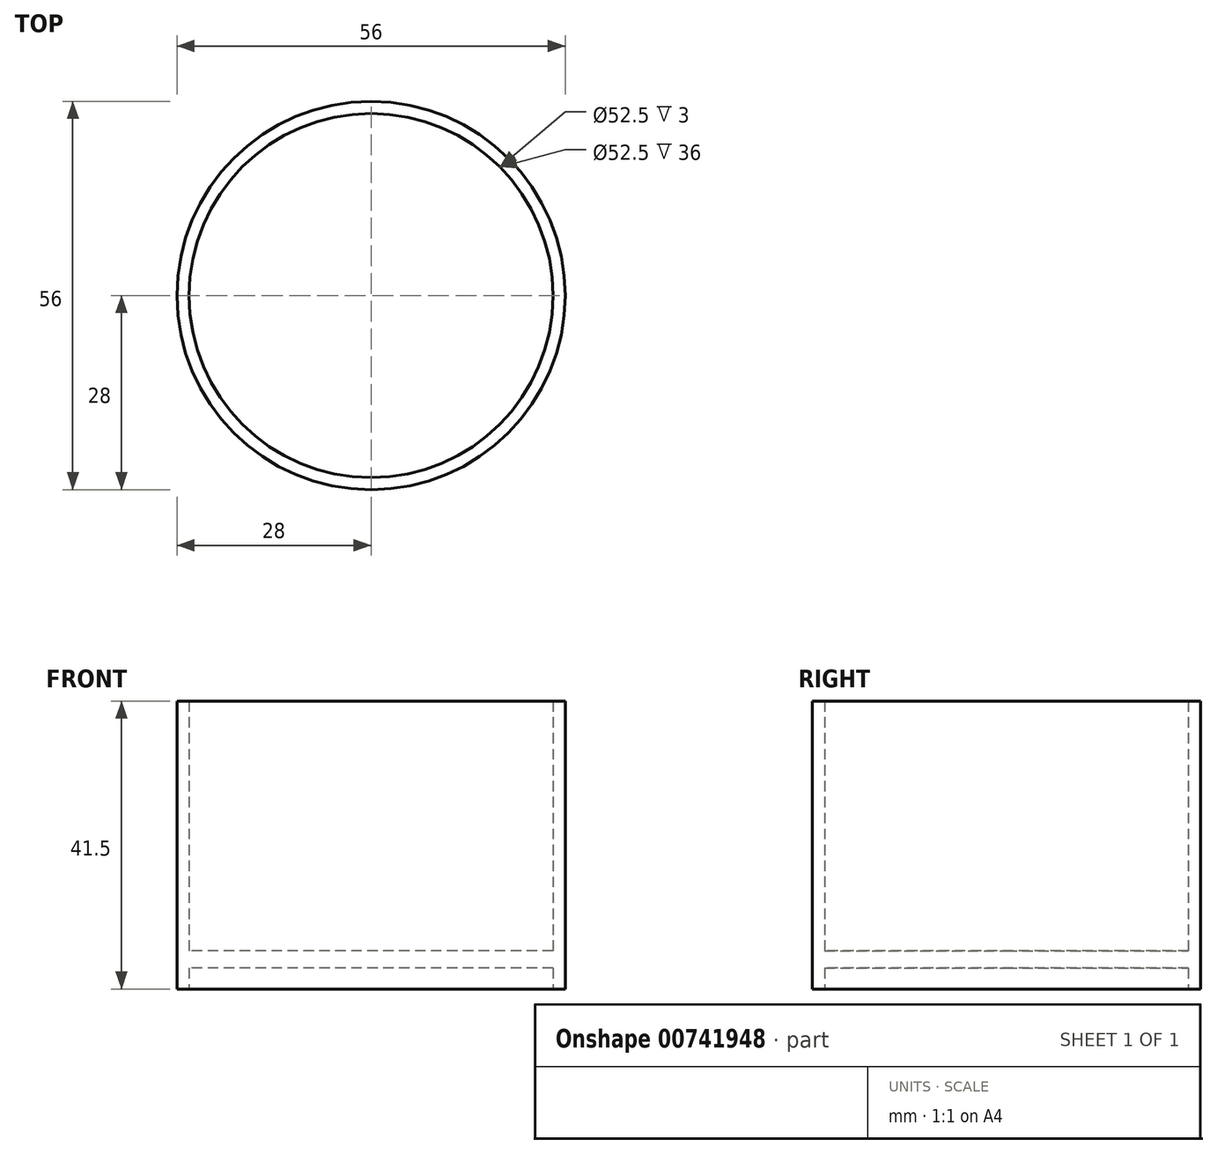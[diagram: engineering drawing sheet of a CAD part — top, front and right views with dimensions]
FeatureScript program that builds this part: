
annotation { "Feature Type Name" : "Feature", "Feature Type Description" : "" }
export const myFeature = defineFeature(function(context is Context, id is Id, definition is map)
    precondition{}
    {
        {
            var Q0;
            Q0=qCreatedBy(makeId("Top.planeOp"),FACE);
            var sketch = newSketch(context, id + "F0", { "sketchPlane" : qUnion([Q0])});
            skCircle(sketch, "E0", {"center": v(0, 0) * mm, "radius": 26.25 * mm});
            skCircle(sketch, "E1", {"center": v(0, 0) * mm, "radius": 28 * mm});
            skSolve(sketch);
        }
        {
            var Q0;
            Q0 = qSketchRegion(id + "F0", true);
            extrude(context, id + "F1", {"entities" : qUnion([Q0]), "depth" : 41.5 * mm, "offsetDistance" : 25 * mm});
        }
        {
            var Q0;
            Q0=qCreatedBy(makeId("Top.planeOp"),FACE);
            cPlane(context, id + "F2", {"entities" : qUnion([Q0]), "cplaneType" : CPlaneType.OFFSET, "offset" : 3 * mm, "width" : 150 * mm, "height" : 150 * mm});
        }
        {
            var Q0;
            Q0=qCreatedBy(id+"F2.planeOp",FACE);
            var sketch = newSketch(context, id + "F3", { "sketchPlane" : qUnion([Q0])});
            skCircle(sketch, "E2.0", {"center": v(0, 0) * mm, "radius": 26.25 * mm});
            skSolve(sketch);
        }
        {
            var Q0;
            Q0 = qSketchRegion(id + "F3", true);
            extrude(context, id + "F4", {"entities" : qUnion([Q0]), "operationType" : NewBodyOperationType.ADD, "depth" : 2.5 * mm, "offsetDistance" : 25 * mm});
        }
    });
